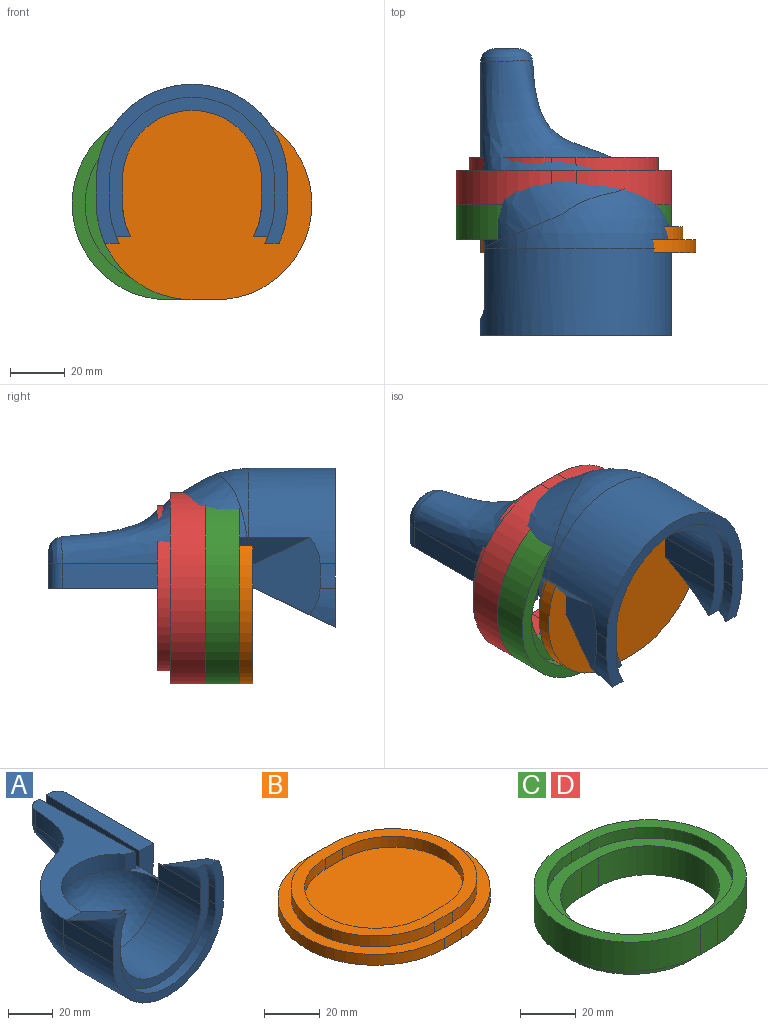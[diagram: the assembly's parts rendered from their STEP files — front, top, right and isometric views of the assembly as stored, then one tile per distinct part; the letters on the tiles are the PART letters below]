
ASSEMBLY  parts=4 mates=5
PART A: 43 faces, bbox 71.7x106.7x60 mm
  f0: cylinder r=25.4mm len=24.73mm, axis (0,1,0), area 154.4mm2, adj f14,f20,f40
  f1: cylinder r=34.92mm len=14.3mm, axis (0,1,0), area 96.8mm2, adj f6,f21,f22,f40
  f2: cylinder r=30.16mm len=14.3mm, axis (0,1,0), area 64.8mm2, adj f6,f14,f19,f40
  f3: plane 17.89x6.45mm, normal (0,0,1), area 32.3mm2, adj f8,f11,f21,f23,f26,f27,f28,f29
  f4: plane 13.72x8.97mm, normal (0,1,0), area 66.1mm2, adj f11,f24,f26,f31,f32,f33,f39,f42
  f5: sphere r=34.92mm, area 1484.5mm2, adj f9,f10,f17,f28,f29
  f6: plane 69.85x58.12mm, normal (0,-1,0), area 712.6mm2, adj f1,f2,f9,f15,f16,f19,f22,f34
  f7: cylinder r=25.4mm len=50.8mm, axis (0,1,0), area 2153.5mm2, adj f8,f13,f14,f20
  f8: sphere r=25.4mm, area 2026.8mm2, adj f3,f7,f12
  f9: cylinder r=34.92mm len=69.85mm, axis (0,1,0), area 3243.9mm2, adj f5,f6,f16,f21,f22,f30
  f10: bspline ~73.03x59.62mm, area 3715.3mm2, adj f5,f18,f23,f25,f28,f32
  f11: plane 60.33x10.47mm, normal (1,0.03,0), area 577.9mm2, adj f3,f4,f26,f27,f39
  f12: cylinder r=25.4mm len=45.42mm, axis (0,0,-1), area 559.7mm2, adj f8,f13,f27,f39
  f13: plane 26.99x8.89mm, normal (1,0,0), area 239.9mm2, adj f7,f12,f14,f35,f39
  f14: plane 60.33x51.04mm, normal (0,-1,0), area 618.5mm2, adj f0,f2,f7,f13,f15,f19,f20,f34
  f15: plane 8.89x4.76mm, normal (1,0,0), area 42.3mm2, adj f6,f14,f34,f37
  f16: plane 31.75x8.89mm, normal (-1,0,0), area 282.3mm2, adj f6,f9,f17,f36,f39
  f17: cylinder r=34.92mm len=24.7mm, axis (0,0,-1), area 243.9mm2, adj f5,f16,f18,f39
  f18: extruded ~43.43x40.49mm, area 577.6mm2, adj f10,f17,f33,f39
  f19: plane 8.89x4.76mm, normal (-1,0,0), area 42.3mm2, adj f2,f6,f14,f34
  f20: plane 26.99x8.89mm, normal (-1,0,0), area 239.9mm2, adj f0,f7,f14,f21,f41
  f21: plane 30.28x28.07mm, normal (0.94,0.34,0), area 509mm2, adj f1,f3,f9,f20,f22,f30,f40,f41
  f22: plane 8.89x5.58mm, normal (1,0,0), area 49.6mm2, adj f1,f6,f9,f21
  f23: plane 18.99x9.31mm, normal (0,-1,0), area 119.8mm2, adj f3,f10,f24,f25,f28,f42
  f24: plane 60.33x10.47mm, normal (-1,0.03,0), area 584.1mm2, adj f4,f23,f26,f42
  f25: plane 55.25x8.89mm, normal (1,0,0), area 491.1mm2, adj f10,f23,f31,f42
  f26: plane 60.33x4.75mm, normal (0,0.03,1), area 191.1mm2, adj f3,f4,f11,f24
  f27: plane 8.89x4.57mm, normal (-0.44,-0.9,0), area 45.2mm2, adj f3,f11,f12,f39
  f28: bspline ~12.38x9.8mm, area 142.6mm2, adj f3,f5,f10,f23,f29
  f29: cone r=26.22mm half-angle=36.9deg, axis (0,0,-1), area 11.4mm2, adj f3,f5,f28,f30
  f30: plane 22.36x9.75mm, normal (0.8,0,0.6), area 150mm2, adj f3,f9,f21,f29
  f31: cylinder r=5.08mm len=8.89mm, axis (0,0,1), area 70.9mm2, adj f4,f25,f32,f42
  f32: bspline ~19.13x14.48mm, area 189.4mm2, adj f4,f10,f31,f33
  f33: cylinder r=5.08mm len=8.89mm, axis (0,0,-1), area 69.4mm2, adj f4,f18,f32,f39
  f34: cylinder r=30.16mm len=60.33mm, axis (0,1,0), area 451.3mm2, adj f6,f14,f15,f19
  f35: cylinder r=25.4mm len=24.73mm, axis (0,1,0), area 154.4mm2, adj f13,f14,f38
  f36: cylinder r=34.92mm len=29.5mm, axis (0,1,0), area 217.3mm2, adj f6,f16,f38
  f37: cylinder r=30.16mm len=14.3mm, axis (0,1,0), area 64.8mm2, adj f6,f14,f15,f38
  f38: plane 30.28x15.09mm, normal (0,0.44,0.9), area 297.1mm2, adj f6,f14,f35,f36,f37,f39
  f39: plane 75.28x59.51mm, normal (0,0,1), area 1282.6mm2, adj f4,f11,f12,f13,f16,f17,f18,f27
  f40: plane 30.28x15.09mm, normal (0,0.44,0.9), area 194.6mm2, adj f0,f1,f2,f6,f14,f21,f41
  f41: plane 2.25x0.82mm, normal (0,0,1), area 0.9mm2, adj f20,f21,f40
  f42: plane 60.33x8.73mm, normal (0,0,1), area 473.5mm2, adj f4,f23,f24,f25,f31
PART B: 16 faces, bbox 78.7x69.9x9.5 mm
  f0: plane 78.74x69.85mm, normal (0,0,1), area 1058.5mm2, adj f1,f2,f3,f4,f6,f7,f8,f13
  f1: plane 8.89x4.76mm, normal (0,-1,0), area 42.3mm2, adj f0,f2,f4,f5
  f2: cylinder r=34.92mm len=69.85mm, axis (0,0,1), area 522.5mm2, adj f0,f1,f3,f5
  f3: plane 8.89x4.76mm, normal (0,1,0), area 42.3mm2, adj f0,f2,f4,f5
  f4: cylinder r=34.92mm len=69.85mm, axis (0,0,1), area 522.5mm2, adj f0,f1,f3,f5
  f5: plane 78.74x69.85mm, normal (0,0,-1), area 4452.9mm2, adj f1,f2,f3,f4
  f6: plane 8.89x4.76mm, normal (0,1,0), area 42.3mm2, adj f0,f7,f13,f14
  f7: cylinder r=30.16mm len=60.33mm, axis (0,0,-1), area 451.3mm2, adj f0,f6,f8,f14
  f8: plane 8.89x4.76mm, normal (0,-1,0), area 42.3mm2, adj f0,f7,f13,f14
  f9: cylinder r=25.4mm len=50.8mm, axis (0,0,-1), area 380mm2, adj f10,f12,f14,f15
  f10: plane 8.89x4.76mm, normal (0,-1,0), area 42.3mm2, adj f9,f11,f14,f15
  f11: cylinder r=25.4mm len=50.8mm, axis (0,0,-1), area 380mm2, adj f10,f12,f14,f15
  f12: plane 8.89x4.76mm, normal (0,1,0), area 42.3mm2, adj f9,f11,f14,f15
  f13: cylinder r=30.16mm len=60.33mm, axis (0,0,-1), area 451.3mm2, adj f0,f6,f8,f14
  f14: plane 69.22x60.33mm, normal (0,0,1), area 916mm2, adj f6,f7,f8,f9,f10,f11,f12,f13
  f15: plane 59.69x50.8mm, normal (0,0,1), area 2478.4mm2, adj f9,f10,f11,f12
PART C: 20 faces, bbox 78.7x69.9x17.5 mm
  f0: plane 12.7x8.89mm, normal (0,-1,0), area 112.9mm2, adj f1,f7,f8,f9
  f1: cylinder r=34.92mm len=69.85mm, axis (0,0,-1), area 1393.4mm2, adj f0,f2,f8,f9
  f2: plane 12.7x8.89mm, normal (0,1,0), area 112.9mm2, adj f1,f7,f8,f9
  f3: cylinder r=30.16mm len=60.33mm, axis (0,0,-1), area 451.3mm2, adj f4,f6,f8,f18
  f4: plane 8.89x4.76mm, normal (0,-1,0), area 42.3mm2, adj f3,f5,f8,f18
  f5: cylinder r=30.16mm len=60.33mm, axis (0,0,-1), area 451.3mm2, adj f4,f6,f8,f18
  f6: plane 8.89x4.76mm, normal (0,1,0), area 42.3mm2, adj f3,f5,f8,f18
  f7: cylinder r=34.92mm len=69.85mm, axis (0,0,-1), area 1393.4mm2, adj f0,f2,f8,f9
  f8: plane 78.74x69.85mm, normal (0,0,1), area 1058.5mm2, adj f0,f1,f2,f3,f4,f5,f6,f7
  f9: plane 78.74x69.85mm, normal (0,0,-1), area 1058.5mm2, adj f0,f1,f2,f7,f10,f11,f12,f13
  f10: plane 8.89x4.76mm, normal (0,1,0), area 42.3mm2, adj f9,f11,f13,f19
  f11: cylinder r=30.16mm len=60.33mm, axis (0,0,-1), area 451.3mm2, adj f9,f10,f12,f19
  f12: plane 8.89x4.76mm, normal (0,-1,0), area 42.3mm2, adj f9,f11,f13,f19
  f13: cylinder r=30.16mm len=60.33mm, axis (0,0,-1), area 451.3mm2, adj f9,f10,f12,f19
  f14: cylinder r=25.4mm len=50.8mm, axis (0,0,-1), area 1013.4mm2, adj f15,f17,f18,f19
  f15: plane 12.7x8.89mm, normal (0,-1,0), area 112.9mm2, adj f14,f16,f18,f19
  f16: cylinder r=25.4mm len=50.8mm, axis (0,0,-1), area 1013.4mm2, adj f15,f17,f18,f19
  f17: plane 12.7x8.89mm, normal (0,1,0), area 112.9mm2, adj f14,f16,f18,f19
  f18: plane 69.22x60.33mm, normal (0,0,1), area 916mm2, adj f3,f4,f5,f6,f14,f15,f16,f17
  f19: plane 69.22x60.33mm, normal (0,0,-1), area 916mm2, adj f10,f11,f12,f13,f14,f15,f16,f17
PART D: same geometry as C
PLACE A rot(axis=(0,-1,0),180deg) t=(-3.88,-2.64,7.1)mm
PLACE B rot(axis=(-1,0,0),90deg) t=(0.57,0.54,-1.79)mm fixed
PLACE C rot(axis=(1,0,0),90deg) t=(-8.32,13.24,-1.79)mm
PLACE D rot(axis=(1,0,0),90deg) t=(-8.32,25.94,-1.79)mm
MATE slider C.f1 <-> D.f1  axis (0,1,0) through (-3.88,18,-1.79)mm
MATE slider D.f1 <-> A.f2  axis (0,1,0) through (-3.88,30.7,-1.79)mm
MATE planar B.f15 <-> C.f8  axis (0,1,0) through (0.57,0.54,-1.79)mm
MATE slider B.f2 <-> C.f1  axis (0,1,0) through (-3.88,0.54,-1.79)mm
MATE planar C.f9 <-> D.f8  axis (0,1,0) through (-8.32,13.24,-1.79)mm
